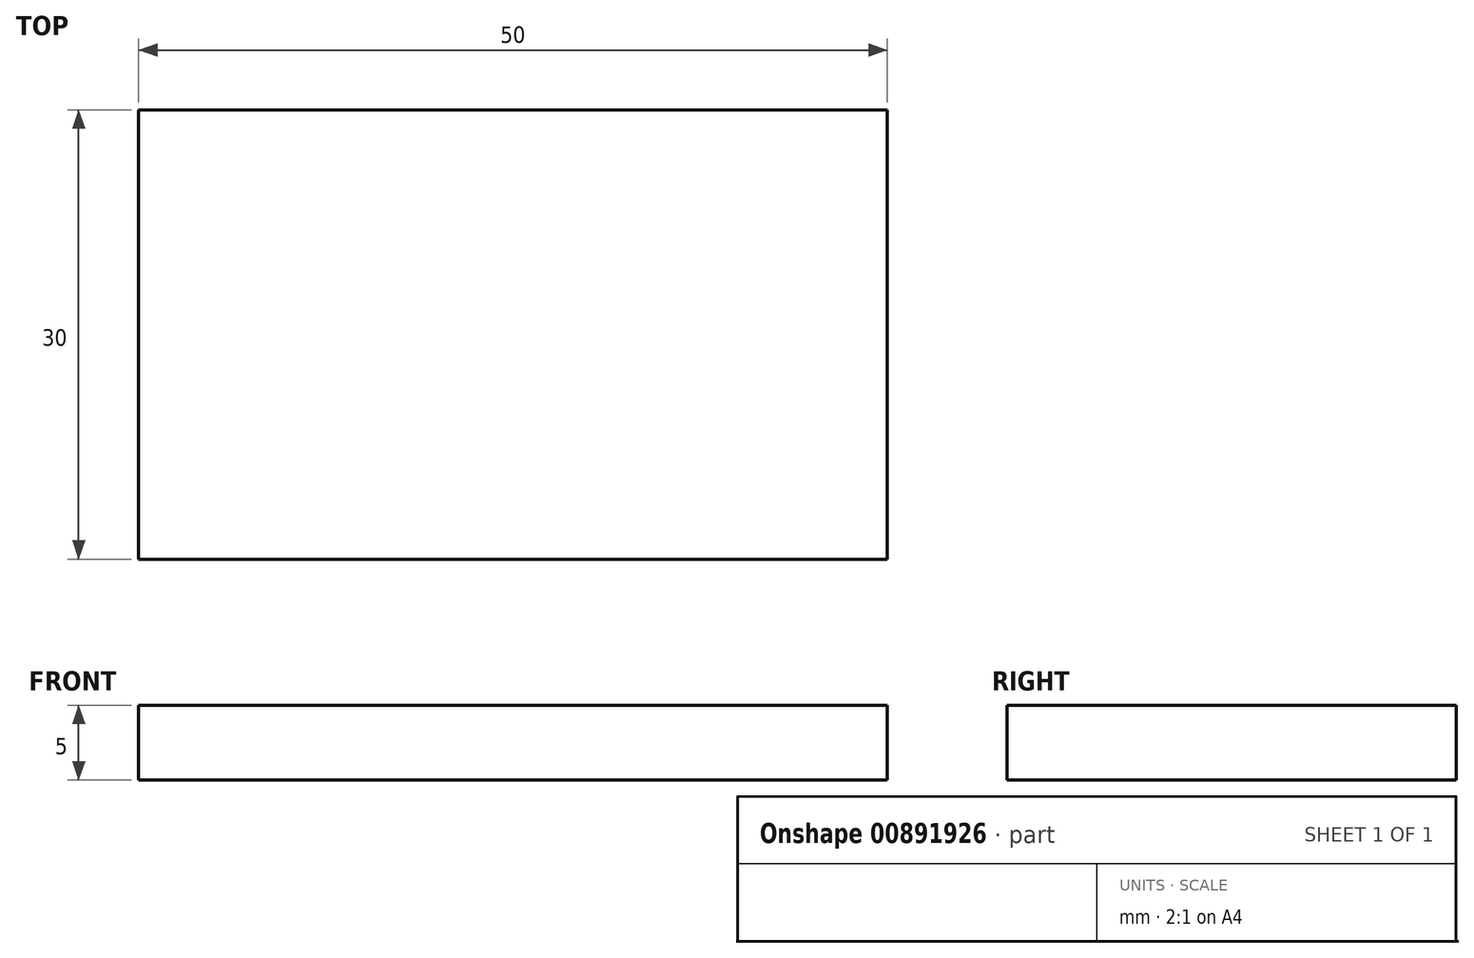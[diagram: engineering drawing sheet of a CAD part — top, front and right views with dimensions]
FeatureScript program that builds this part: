
annotation { "Feature Type Name" : "Feature", "Feature Type Description" : "" }
export const myFeature = defineFeature(function(context is Context, id is Id, definition is map)
    precondition{}
    {
        {
            var Q0;
            Q0=qCreatedBy(makeId("Top.planeOp"),FACE);
            var sketch = newSketch(context, id + "F0", { "sketchPlane" : qUnion([Q0])});
            skLineSegment(sketch, "E0.bottom", {"start": v(25, -15) * mm, "end": v(-25, -15) * mm});
            skLineSegment(sketch, "E0.top", {"start": v(25, 15) * mm, "end": v(-25, 15) * mm});
            skLineSegment(sketch, "E0.left", {"start": v(25, -15) * mm, "end": v(25, 15) * mm});
            skLineSegment(sketch, "E0.right", {"start": v(-25, -15) * mm, "end": v(-25, 15) * mm});
            skPoint(sketch, "E0.middle", {"position": v(0, 0) * mm});
            skSolve(sketch);
        }
        {
            var Q0;
            Q0 = qSketchRegion(id + "F0", true);
            extrude(context, id + "F1", {"entities" : qUnion([Q0]), "depth" : 5 * mm, "offsetDistance" : 25 * mm});
        }
    });
